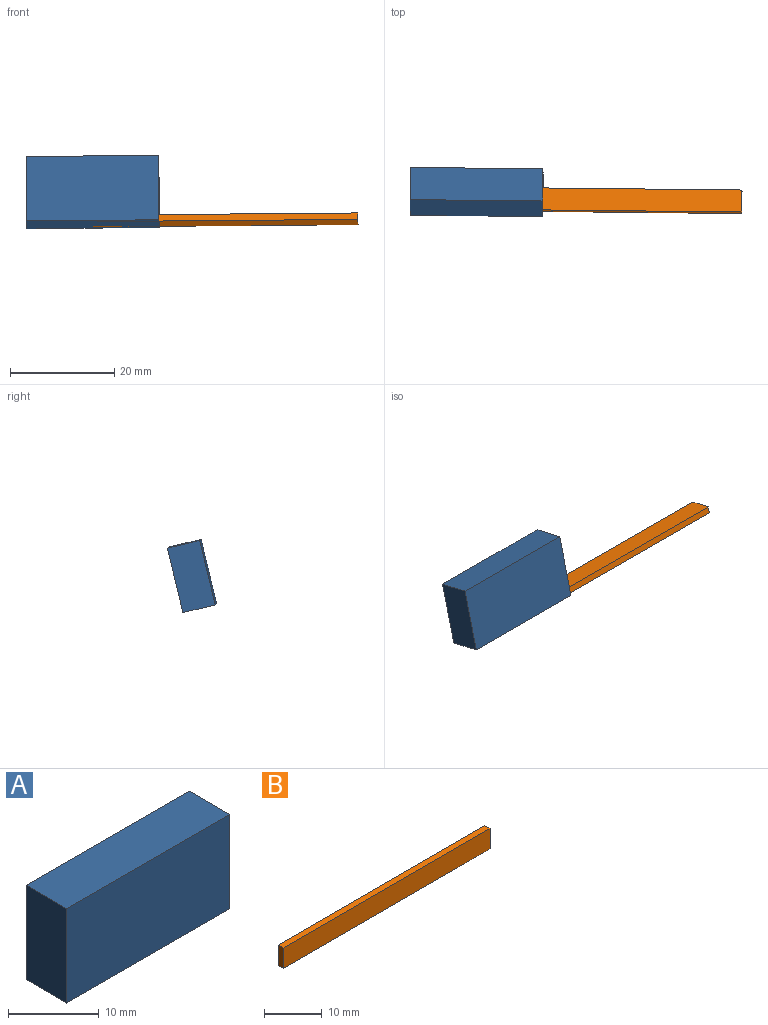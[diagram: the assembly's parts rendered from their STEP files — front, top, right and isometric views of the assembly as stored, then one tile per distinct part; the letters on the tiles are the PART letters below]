
ASSEMBLY  parts=2 mates=1
PART A: 6 faces, bbox 25.4x6.4x12.7 mm
  f0: plane 25.4x6.35mm, normal (0,0,1), area 161.3mm2, adj f1,f3,f4,f5
  f1: plane 12.7x6.35mm, normal (-1,0,0), area 80.6mm2, adj f0,f2,f4,f5
  f2: plane 25.4x6.35mm, normal (0,0,-1), area 161.3mm2, adj f1,f3,f4,f5
  f3: plane 12.7x6.35mm, normal (1,0,0), area 80.6mm2, adj f0,f2,f4,f5
  f4: plane 25.4x12.7mm, normal (0,-1,0), area 322.6mm2, adj f0,f1,f2,f3
  f5: plane 25.4x12.7mm, normal (0,1,0), area 322.6mm2, adj f0,f1,f2,f3
PART B: 6 faces, bbox 50.8x1.3x4.3 mm
  f0: plane 4.34x1.27mm, normal (-1,0,0), area 5.5mm2, adj f1,f3,f4,f5
  f1: plane 50.8x1.27mm, normal (0,0,-1), area 64.5mm2, adj f0,f2,f4,f5
  f2: plane 4.34x1.27mm, normal (1,0,0), area 5.5mm2, adj f1,f3,f4,f5
  f3: plane 50.8x1.27mm, normal (0,0,1), area 64.5mm2, adj f0,f2,f4,f5
  f4: plane 50.8x4.34mm, normal (0,-1,0), area 220.2mm2, adj f0,f1,f2,f3
  f5: plane 50.8x4.34mm, normal (0,1,0), area 220.2mm2, adj f0,f1,f2,f3
PLACE A rot(axis=(-1,-0.03,-0.05),13.5deg) t=(20.41,1.3,-14.62)mm
PLACE B rot(axis=(-1,0,-0.01),103.5deg) t=(83.36,-42.22,-3.17)mm
MATE fastened A.f2 <-> B.f5  axis (0.01,-0.23,-0.97) through (33.07,-1.92,-13.77)mm
